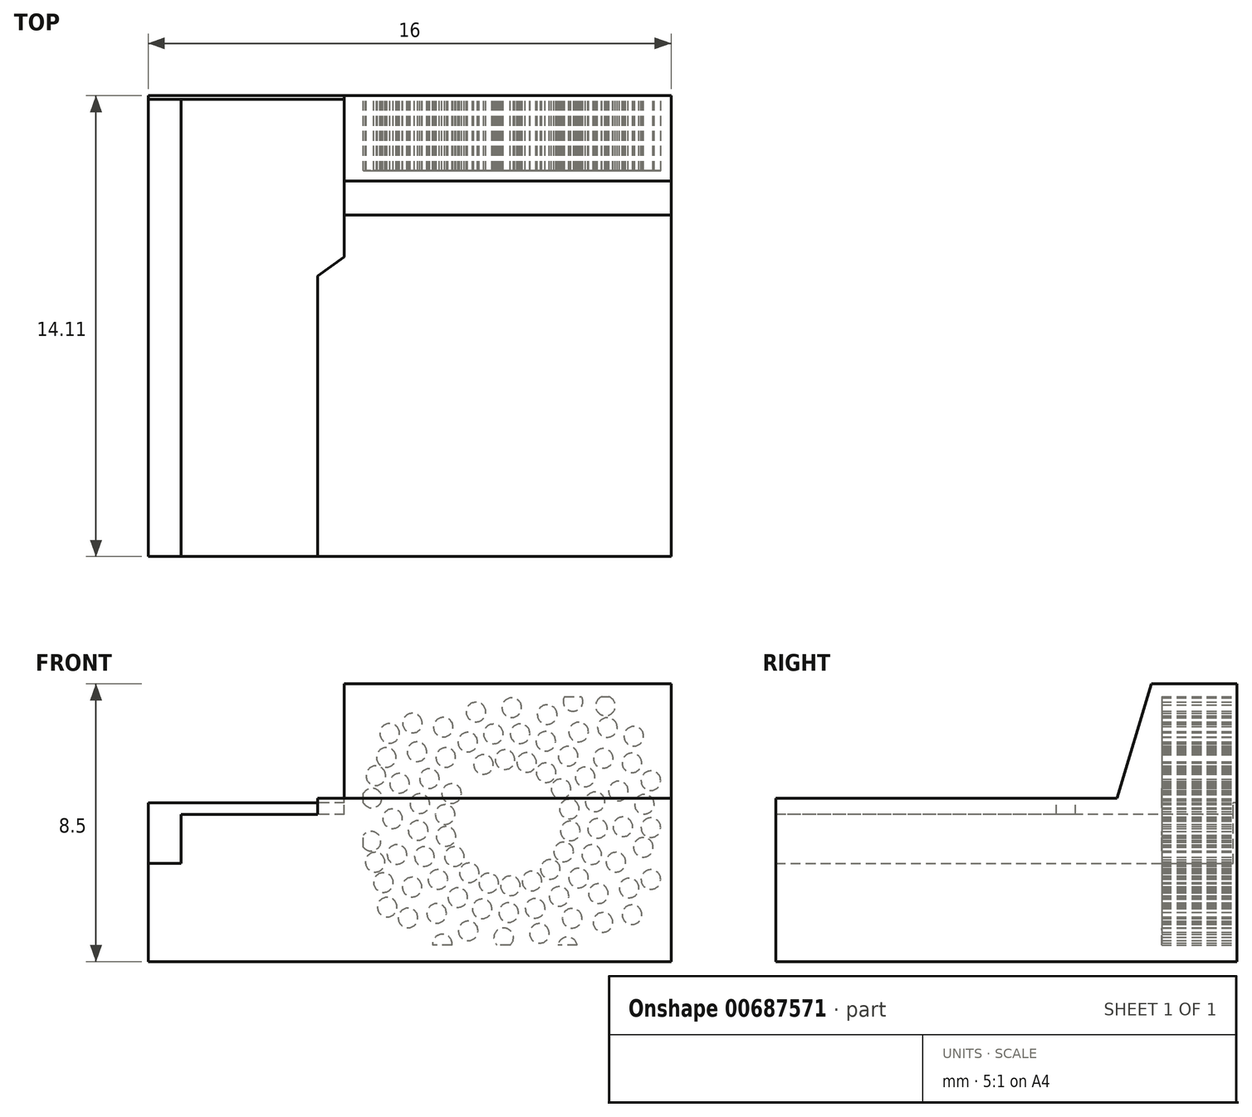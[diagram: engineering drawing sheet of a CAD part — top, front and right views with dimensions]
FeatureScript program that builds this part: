
annotation { "Feature Type Name" : "Feature", "Feature Type Description" : "" }
export const myFeature = defineFeature(function(context is Context, id is Id, definition is map)
    precondition{}
    {
        {
            var Q0;
            Q0=qCreatedBy(makeId("Top.planeOp"),FACE);
            var sketch = newSketch(context, id + "F0", { "sketchPlane" : qUnion([Q0])});
            skLineSegment(sketch, "E0.bottom", {"start": v(0, 0) * mm, "end": v(-16, 0) * mm});
            skLineSegment(sketch, "E0.top", {"start": v(0, 14) * mm, "end": v(-16, 14) * mm});
            skLineSegment(sketch, "E0.left", {"start": v(0, 0) * mm, "end": v(0, 14) * mm});
            skLineSegment(sketch, "E0.right", {"start": v(-16, 0) * mm, "end": v(-16, 14) * mm});
            skSolve(sketch);
        }
        {
            var Q0;
            Q0 = qSketchRegion(id + "F0", true);
            extrude(context, id + "F1", {"entities" : qUnion([Q0]), "depth" : 5 * mm, "offsetDistance" : 25 * mm});
        }
        {
            var Q0;
            Q0=makeQuery(id+"F1.opExtrude","CAP_FACE",FACE,{"disambiguationData":[OSD([sQuery(id+"F0.wireOp",EDGE,"E0.bottom"),sQuery(id+"F0.wireOp",EDGE,"E0.top"),sQuery(id+"F0.wireOp",EDGE,"E0.left"),sQuery(id+"F0.wireOp",EDGE,"E0.right")])],"isStart":false});
            var sketch = newSketch(context, id + "F2", { "sketchPlane" : qUnion([Q0])});
            skLineSegment(sketch, "E1.bottom", {"start": v(-16, 14) * mm, "end": v(-15, 14) * mm});
            skLineSegment(sketch, "E1.top", {"start": v(-16, 0) * mm, "end": v(-15, 0) * mm});
            skLineSegment(sketch, "E1.left", {"start": v(-16, 14) * mm, "end": v(-16, 0) * mm});
            skLineSegment(sketch, "E1.right", {"start": v(-15, 14) * mm, "end": v(-15, 0) * mm});
            skSolve(sketch);
        }
        {
            var Q0;
            Q0=makeQuery(id+"F2.imprint","IMPRINT",FACE,{"disambiguationData":[TD([[makeQuery(id+"F2.imprint","IMPRINT",EDGE,{"derivedFrom":sQuery(id+"F2.wireOp",EDGE,"E1.bottom")}),1.0]])]});
            extrude(context, id + "F3", {"entities" : qUnion([Q0]), "operationType" : NewBodyOperationType.REMOVE, "oppositeDirection" : true, "depth" : 2 * mm, "offsetDistance" : 25 * mm});
        }
        {
            var Q0;
            Q0=makeQuery(id+"F1.opExtrude","CAP_FACE",FACE,{"disambiguationData":[OSD([sQuery(id+"F0.wireOp",EDGE,"E0.bottom"),sQuery(id+"F0.wireOp",EDGE,"E0.top"),sQuery(id+"F0.wireOp",EDGE,"E0.left"),sQuery(id+"F0.wireOp",EDGE,"E0.right")])],"isStart":false});
            var sketch = newSketch(context, id + "F4", { "sketchPlane" : qUnion([Q0])});
            skLineSegment(sketch, "E2", {"start": v(-15, 14) * mm, "end": v(-10, 14) * mm});
            skLineSegment(sketch, "E3", {"start": v(-10, 14) * mm, "end": v(-10, 9.18) * mm});
            skLineSegment(sketch, "E4", {"start": v(-10, 9.18) * mm, "end": v(-10.81, 8.6) * mm});
            skLineSegment(sketch, "E5", {"start": v(-10.81, 8.6) * mm, "end": v(-10.81, 0) * mm});
            skLineSegment(sketch, "E6", {"start": v(-15, 14) * mm, "end": v(-15, 0) * mm});
            skLineSegment(sketch, "E7", {"start": v(-15, 0) * mm, "end": v(-10.81, 0) * mm});
            skSolve(sketch);
        }
        {
            var Q0;
            Q0 = qSketchRegion(id + "F4", true);
            extrude(context, id + "F5", {"entities" : qUnion([Q0]), "operationType" : NewBodyOperationType.REMOVE, "endBound" : BoundingType.SYMMETRIC, "oppositeDirection" : true, "depth" : 1 * mm, "offsetDistance" : 25 * mm});
        }
        {
            var Q0;
            Q0=makeQuery(id+"F1.opExtrude","CAP_FACE",FACE,{"disambiguationData":[OSD([sQuery(id+"F0.wireOp",EDGE,"E0.bottom"),sQuery(id+"F0.wireOp",EDGE,"E0.top"),sQuery(id+"F0.wireOp",EDGE,"E0.left"),sQuery(id+"F0.wireOp",EDGE,"E0.right")])],"isStart":false});
            var sketch = newSketch(context, id + "F6", { "sketchPlane" : qUnion([Q0])});
            skLineSegment(sketch, "E8", {"start": v(0, 14) * mm, "end": v(0, 10) * mm});
            skLineSegment(sketch, "E9", {"start": v(0, 10) * mm, "end": v(-10, 10) * mm});
            skLineSegment(sketch, "E10", {"start": v(-10, 10) * mm, "end": v(-10, 14) * mm});
            skLineSegment(sketch, "E11", {"start": v(-10, 14) * mm, "end": v(0, 14) * mm});
            skSolve(sketch);
        }
        {
            var Q0;
            Q0=makeQuery(id+"F6.imprint","IMPRINT",FACE,{"disambiguationData":[TD([[makeQuery(id+"F6.imprint","IMPRINT",EDGE,{"derivedFrom":sQuery(id+"F6.wireOp",EDGE,"E8")}),1.0]])]});
            extrude(context, id + "F7", {"entities" : qUnion([Q0]), "operationType" : NewBodyOperationType.ADD, "depth" : 3.5 * mm, "offsetDistance" : 25 * mm});
        }
        {
            var Q0;
            Q0=makeQuery(id+"F7.opExtrude","CAP_EDGE",EDGE,{"disambiguationData":[OSD([sQuery(id+"F6.wireOp",EDGE,"E9")])],"isStart":false});
            chamfer(context, id + "F8", {"entities" : qUnion([Q0]), "chamferType" : ChamferType.TWO_OFFSETS, "width1" : 5 * mm, "oppositeDirection" : false, "width2" : 1.5 * mm, "tangentPropagation" : true});
        }
        {
            var Q0;
            Q0=makeQuery(id+"F7.boolean.opBoolean","MERGE",FACE,{"derivedFrom":[makeQuery(id+"F1.opExtrude","SWEPT_FACE",FACE,{"disambiguationData":[OSD([sQuery(id+"F0.wireOp",EDGE,"E0.top")])]}),makeQuery(id+"F7.opExtrude","SWEPT_FACE",FACE,{"disambiguationData":[OSD([sQuery(id+"F6.wireOp",EDGE,"E11")])]})]});
            var sketch = newSketch(context, id + "F9", { "sketchPlane" : qUnion([Q0])});
            skLineSegment(sketch, "E12", {"start": v(10, 4.85) * mm, "end": v(15, 4.85) * mm});
            skLineSegment(sketch, "E13", {"start": v(16, 3) * mm, "end": v(16, 4.85) * mm});
            skLineSegment(sketch, "E14", {"start": v(16, 4.85) * mm, "end": v(15, 4.85) * mm});
            skLineSegment(sketch, "E15", {"start": v(10, 4.85) * mm, "end": v(10, 0) * mm});
            skLineSegment(sketch, "E16", {"start": v(10, 0) * mm, "end": v(16, 0) * mm});
            skLineSegment(sketch, "E17", {"start": v(16, 0) * mm, "end": v(16, 3) * mm});
            skSolve(sketch);
        }
        {
            var Q0;
            Q0 = qSketchRegion(id + "F9", true);
            var Q1;
            {var subQ0=sQuery(id+"F6.wireOp",EDGE,"E11");var subQ1=makeQuery(id+"F7.opExtrude","CAP_EDGE",EDGE,{"disambiguationData":[OSD([subQ0])],"isStart":false});Q1=makeQuery(id+"F9.imprint","IMPRINT",FACE,{"disambiguationData":[TD([[makeQuery(id+"F9.imprint","IMPRINT",EDGE,{"derivedFrom":subQ1}),-1.0]])]});}
            extrude(context, id + "F10", {"entities" : qUnion([Q0, Q1]), "operationType" : NewBodyOperationType.ADD, "depth" : 0.1 * mm, "offsetDistance" : 25 * mm});
        }
        {
            var Q0;
            Q0=makeQuery(id+"F10.opExtrude","CAP_FACE",FACE,{"disambiguationData":[OSD([sQuery(id+"F0.wireOp",EDGE,"E0.top"),sQuery(id+"F0.wireOp",EDGE,"E0.left"),sQuery(id+"F4.wireOp",EDGE,"E2"),sQuery(id+"F4.wireOp",EDGE,"E3"),sQuery(id+"F6.wireOp",EDGE,"E8"),sQuery(id+"F6.wireOp",EDGE,"E10"),sQuery(id+"F6.wireOp",EDGE,"E11"),sQuery(id+"F9.wireOp",EDGE,"E12"),sQuery(id+"F9.wireOp",EDGE,"E13"),sQuery(id+"F9.wireOp",EDGE,"E14"),sQuery(id+"F9.wireOp",EDGE,"E16"),sQuery(id+"F9.wireOp",EDGE,"E17")])],"isStart":false});
            var sketch = newSketch(context, id + "F11", { "sketchPlane" : qUnion([Q0])});
            skCircle(sketch, "E18.cCircle", {"center": v(5, 4.25) * mm, "radius": 1.07 * mm, "construction": true});
            skPoint(sketch, "E18.cCircle.centerSnap0", {"position": v(0, 4.25) * mm});
            skPoint(sketch, "E18.cCircle.centerSnap1", {"position": v(5, 8.5) * mm});
            skLineSegment(sketch, "E18.0", {"start": v(6.23, 4.28) * mm, "end": v(5.64, 3.2) * mm});
            skLineSegment(sketch, "E18.1", {"start": v(5.64, 3.2) * mm, "end": v(4.4, 3.17) * mm});
            skLineSegment(sketch, "E18.2", {"start": v(4.4, 3.17) * mm, "end": v(3.77, 4.22) * mm});
            skLineSegment(sketch, "E18.3", {"start": v(3.77, 4.22) * mm, "end": v(4.36, 5.3) * mm});
            skLineSegment(sketch, "E18.4", {"start": v(4.36, 5.3) * mm, "end": v(5.6, 5.33) * mm});
            skLineSegment(sketch, "E18.5", {"start": v(5.6, 5.33) * mm, "end": v(6.23, 4.28) * mm});
            skPoint(sketch, "E18.0.midPoint", {"position": v(5.94, 3.74) * mm});
            skLineSegment(sketch, "E19", {"start": v(4.98, 8.1) * mm, "end": v(1.66, 8.1) * mm});
            skPoint(sketch, "E19.startSnap0", {"position": v(4.98, 5.32) * mm});
            skLineSegment(sketch, "E20", {"start": v(1.66, 8.1) * mm, "end": v(0.32, 6.97) * mm});
            skLineSegment(sketch, "E21", {"start": v(0.32, 6.97) * mm, "end": v(0.32, 1.53) * mm});
            skLineSegment(sketch, "E22", {"start": v(0.32, 1.53) * mm, "end": v(1.39, 0.5) * mm});
            skLineSegment(sketch, "E23", {"start": v(1.39, 0.5) * mm, "end": v(8.08, 0.5) * mm});
            skLineSegment(sketch, "E24", {"start": v(8.08, 0.5) * mm, "end": v(9.41, 1.53) * mm});
            skLineSegment(sketch, "E25", {"start": v(9.41, 1.53) * mm, "end": v(9.41, 6.97) * mm});
            skLineSegment(sketch, "E26", {"start": v(9.41, 6.97) * mm, "end": v(7.8, 8.1) * mm});
            skLineSegment(sketch, "E27", {"start": v(7.8, 8.1) * mm, "end": v(4.98, 8.1) * mm});
            skCircle(sketch, "E28", {"center": v(2.63, 5.65) * mm, "radius": 0.3 * mm});
            skCircle(sketch, "E29.1.0", {"center": v(2.32, 4.9) * mm, "radius": 0.3 * mm});
            skCircle(sketch, "E29.2.0", {"center": v(2.25, 4.07) * mm, "radius": 0.3 * mm});
            skCircle(sketch, "E30", {"center": v(3.29, 3.36) * mm, "radius": 0.3 * mm});
            skCircle(sketch, "E31.1.0", {"center": v(3.7, 2.82) * mm, "radius": 0.3 * mm});
            skCircle(sketch, "E31.2.0", {"center": v(4.26, 2.46) * mm, "radius": 0.3 * mm});
            skCircle(sketch, "E32.1.3.0", {"center": v(2.43, 3.27) * mm, "radius": 0.3 * mm});
            skCircle(sketch, "E32.1.4.0", {"center": v(2.83, 2.56) * mm, "radius": 0.3 * mm});
            skCircle(sketch, "E32.1.5.0", {"center": v(3.43, 2) * mm, "radius": 0.3 * mm});
            skCircle(sketch, "E33.1.6.0", {"center": v(4.16, 1.63) * mm, "radius": 0.3 * mm});
            skCircle(sketch, "E33.1.7.0", {"center": v(4.97, 1.5) * mm, "radius": 0.3 * mm});
            skCircle(sketch, "E34.1.3.0", {"center": v(4.92, 2.32) * mm, "radius": 0.3 * mm});
            skCircle(sketch, "E34.1.4.0", {"center": v(5.58, 2.4) * mm, "radius": 0.3 * mm});
            skCircle(sketch, "E34.1.5.0", {"center": v(6.18, 2.72) * mm, "radius": 0.3 * mm});
            skCircle(sketch, "E34.1.6.0", {"center": v(6.63, 3.21) * mm, "radius": 0.3 * mm});
            skCircle(sketch, "E34.1.7.0", {"center": v(6.89, 3.83) * mm, "radius": 0.3 * mm});
            skCircle(sketch, "E35.1.8.0", {"center": v(5.78, 1.61) * mm, "radius": 0.3 * mm});
            skCircle(sketch, "E35.1.9.0", {"center": v(6.53, 1.96) * mm, "radius": 0.3 * mm});
            skCircle(sketch, "E35.1.10.0", {"center": v(7.13, 2.51) * mm, "radius": 0.3 * mm});
            skCircle(sketch, "E35.1.11.0", {"center": v(7.55, 3.22) * mm, "radius": 0.3 * mm});
            skCircle(sketch, "E36.1.12.0", {"center": v(7.74, 4.01) * mm, "radius": 0.3 * mm});
            skCircle(sketch, "E36.1.13.0", {"center": v(7.69, 4.83) * mm, "radius": 0.3 * mm});
            skCircle(sketch, "E36.1.14.0", {"center": v(7.4, 5.6) * mm, "radius": 0.3 * mm});
            skCircle(sketch, "E36.1.15.0", {"center": v(6.9, 6.25) * mm, "radius": 0.3 * mm});
            skCircle(sketch, "E36.1.16.0", {"center": v(6.22, 6.72) * mm, "radius": 0.3 * mm});
            skCircle(sketch, "E36.1.17.0", {"center": v(5.44, 6.97) * mm, "radius": 0.3 * mm});
            skCircle(sketch, "E36.1.18.0", {"center": v(4.62, 6.98) * mm, "radius": 0.3 * mm});
            skCircle(sketch, "E36.1.19.0", {"center": v(3.83, 6.74) * mm, "radius": 0.3 * mm});
            skCircle(sketch, "E37.1.8.0", {"center": v(6.92, 4.5) * mm, "radius": 0.3 * mm});
            skCircle(sketch, "E37.1.9.0", {"center": v(6.71, 5.14) * mm, "radius": 0.3 * mm});
            skCircle(sketch, "E37.1.10.0", {"center": v(6.3, 5.68) * mm, "radius": 0.3 * mm});
            skCircle(sketch, "E37.1.11.0", {"center": v(5.74, 6.04) * mm, "radius": 0.3 * mm});
            skCircle(sketch, "E37.1.12.0", {"center": v(5.08, 6.18) * mm, "radius": 0.3 * mm});
            skCircle(sketch, "E37.1.13.0", {"center": v(4.42, 6.1) * mm, "radius": 0.3 * mm});
            skCircle(sketch, "E37.1.14.0", {"center": v(3.82, 5.78) * mm, "radius": 0.3 * mm});
            skCircle(sketch, "E37.1.15.0", {"center": v(3.37, 5.29) * mm, "radius": 0.3 * mm});
            skCircle(sketch, "E37.1.16.0", {"center": v(3.11, 4.67) * mm, "radius": 0.3 * mm});
            skCircle(sketch, "E37.1.17.0", {"center": v(3.08, 4) * mm, "radius": 0.3 * mm});
            skCircle(sketch, "E38.1.20.0", {"center": v(3.15, 6.29) * mm, "radius": 0.3 * mm});
            skCircle(sketch, "E39", {"center": v(3.8, 7.56) * mm, "radius": 0.3 * mm});
            skCircle(sketch, "E40.1.0", {"center": v(2.83, 7.03) * mm, "radius": 0.3 * mm});
            skCircle(sketch, "E40.2.0", {"center": v(2.08, 6.22) * mm, "radius": 0.3 * mm});
            skCircle(sketch, "E41.1.3.0", {"center": v(1.61, 5.22) * mm, "radius": 0.3 * mm});
            skCircle(sketch, "E41.1.4.0", {"center": v(1.48, 4.13) * mm, "radius": 0.3 * mm});
            skCircle(sketch, "E41.1.5.0", {"center": v(1.69, 3.04) * mm, "radius": 0.3 * mm});
            skCircle(sketch, "E41.1.6.0", {"center": v(2.22, 2.08) * mm, "radius": 0.3 * mm});
            skCircle(sketch, "E41.1.7.0", {"center": v(3.03, 1.33) * mm, "radius": 0.3 * mm});
            skCircle(sketch, "E42.1.8.0", {"center": v(4.03, 0.86) * mm, "radius": 0.3 * mm});
            skArc(sketch, "E42.1.9.0", {"start": v(5.33, 0.5) * mm, "mid": v(5.12, 1.03) * mm, "end": v(4.92, 0.5) * mm});
            skCircle(sketch, "E42.1.10.0", {"center": v(6.2, 0.94) * mm, "radius": 0.3 * mm});
            skCircle(sketch, "E42.1.11.0", {"center": v(7.17, 1.47) * mm, "radius": 0.3 * mm});
            skCircle(sketch, "E42.1.12.0", {"center": v(7.92, 2.28) * mm, "radius": 0.3 * mm});
            skCircle(sketch, "E42.1.13.0", {"center": v(8.39, 3.28) * mm, "radius": 0.3 * mm});
            skCircle(sketch, "E42.1.14.0", {"center": v(8.52, 4.37) * mm, "radius": 0.3 * mm});
            skCircle(sketch, "E42.1.15.0", {"center": v(8.31, 5.46) * mm, "radius": 0.3 * mm});
            skCircle(sketch, "E42.1.16.0", {"center": v(7.78, 6.42) * mm, "radius": 0.3 * mm});
            skCircle(sketch, "E42.1.17.0", {"center": v(6.97, 7.17) * mm, "radius": 0.3 * mm});
            skCircle(sketch, "E42.1.18.0", {"center": v(5.97, 7.64) * mm, "radius": 0.3 * mm});
            skCircle(sketch, "E42.1.19.0", {"center": v(4.88, 7.77) * mm, "radius": 0.3 * mm});
            skArc(sketch, "E43", {"start": v(2.74, 8.1) * mm, "mid": v(3, 7.67) * mm, "end": v(3.27, 8.1) * mm});
            skCircle(sketch, "E44.1.0", {"center": v(1.95, 7.17) * mm, "radius": 0.3 * mm});
            skCircle(sketch, "E44.2.0", {"center": v(1.2, 6.08) * mm, "radius": 0.3 * mm});
            skCircle(sketch, "E45.1.3.0", {"center": v(0.82, 4.82) * mm, "radius": 0.3 * mm});
            skCircle(sketch, "E45.1.4.0", {"center": v(0.85, 3.5) * mm, "radius": 0.3 * mm});
            skCircle(sketch, "E45.1.5.0", {"center": v(1.28, 2.25) * mm, "radius": 0.3 * mm});
            skCircle(sketch, "E45.1.6.0", {"center": v(2.08, 1.2) * mm, "radius": 0.3 * mm});
            skArc(sketch, "E45.1.7.0", {"start": v(3.46, 0.5) * mm, "mid": v(3.17, 0.75) * mm, "end": v(2.87, 0.5) * mm});
            skArc(sketch, "E45.1.10.0", {"start": v(7.3, 0.5) * mm, "mid": v(7, 0.83) * mm, "end": v(6.7, 0.5) * mm});
            skCircle(sketch, "E45.1.11.0", {"center": v(8.05, 1.33) * mm, "radius": 0.3 * mm});
            skCircle(sketch, "E45.1.12.0", {"center": v(8.8, 2.42) * mm, "radius": 0.3 * mm});
            skArc(sketch, "E45.1.13.0", {"start": v(9.41, 3.87) * mm, "mid": v(8.88, 3.68) * mm, "end": v(9.41, 3.5) * mm});
            skArc(sketch, "E45.1.14.0", {"start": v(9.41, 5.15) * mm, "mid": v(8.85, 5) * mm, "end": v(9.41, 4.86) * mm});
            skCircle(sketch, "E45.1.15.0", {"center": v(8.72, 6.25) * mm, "radius": 0.3 * mm});
            skCircle(sketch, "E45.1.16.0", {"center": v(7.92, 7.3) * mm, "radius": 0.3 * mm});
            skArc(sketch, "E45.1.17.0", {"start": v(6.54, 8.1) * mm, "mid": v(6.83, 7.75) * mm, "end": v(7.13, 8.1) * mm});
            skArc(sketch, "E45.1.19.0", {"start": v(4.2, 8.1) * mm, "mid": v(4.25, 8.1) * mm, "end": v(4.3, 8.1) * mm});
            skCircle(sketch, "E46", {"center": v(1.14, 6.9) * mm, "radius": 0.3 * mm});
            skCircle(sketch, "E47", {"center": v(8.61, 6.99) * mm, "radius": 0.3 * mm});
            skCircle(sketch, "E48", {"center": v(8.69, 1.67) * mm, "radius": 0.3 * mm});
            skCircle(sketch, "E49", {"center": v(1.2, 1.43) * mm, "radius": 0.3 * mm});
            skCircle(sketch, "E50", {"center": v(2, 7.83) * mm, "radius": 0.3 * mm});
            skCircle(sketch, "E51", {"center": v(0.62, 5.54) * mm, "radius": 0.3 * mm});
            skCircle(sketch, "E52", {"center": v(9.04, 5.7) * mm, "radius": 0.3 * mm});
            skCircle(sketch, "E53", {"center": v(0.62, 2.51) * mm, "radius": 0.3 * mm});
            skCircle(sketch, "E54", {"center": v(0.62, 4.1) * mm, "radius": 0.3 * mm});
            skCircle(sketch, "E55", {"center": v(9.05, 3.04) * mm, "radius": 0.3 * mm});
            skSolve(sketch);
        }
        {
            var Q0;
            Q0=makeQuery(id+"F11.imprint","IMPRINT",FACE,{"disambiguationData":[TD([[makeQuery(id+"F11.imprint","IMPRINT",EDGE,{"derivedFrom":sQuery(id+"F11.wireOp",EDGE,"E44.1.0")}),1.0]])]});
            var Q1;
            Q1=makeQuery(id+"F11.imprint","IMPRINT",FACE,{"disambiguationData":[TD([[makeQuery(id+"F11.imprint","IMPRINT",EDGE,{"derivedFrom":sQuery(id+"F11.wireOp",EDGE,"E40.1.0")}),1.0]])]});
            var Q2;
            Q2=makeQuery(id+"F11.imprint","IMPRINT",FACE,{"disambiguationData":[TD([[makeQuery(id+"F11.imprint","IMPRINT",EDGE,{"derivedFrom":sQuery(id+"F11.wireOp",EDGE,"E42.1.19.0")}),1.0]])]});
            var Q3;
            Q3=makeQuery(id+"F11.imprint","IMPRINT",FACE,{"disambiguationData":[TD([[makeQuery(id+"F11.imprint","IMPRINT",EDGE,{"derivedFrom":sQuery(id+"F11.wireOp",EDGE,"E38.1.20.0")}),1.0]])]});
            var Q4;
            Q4=makeQuery(id+"F11.imprint","IMPRINT",FACE,{"disambiguationData":[TD([[makeQuery(id+"F11.imprint","IMPRINT",EDGE,{"derivedFrom":sQuery(id+"F11.wireOp",EDGE,"E40.2.0")}),1.0]])]});
            var Q5;
            Q5=makeQuery(id+"F11.imprint","IMPRINT",FACE,{"disambiguationData":[TD([[makeQuery(id+"F11.imprint","IMPRINT",EDGE,{"derivedFrom":sQuery(id+"F11.wireOp",EDGE,"E53")}),1.0]])]});
            var Q6;
            Q6=makeQuery(id+"F11.imprint","IMPRINT",FACE,{"disambiguationData":[TD([[makeQuery(id+"F11.imprint","IMPRINT",EDGE,{"derivedFrom":sQuery(id+"F11.wireOp",EDGE,"E45.1.5.0")}),1.0]])]});
            var Q7;
            Q7=makeQuery(id+"F11.imprint","IMPRINT",FACE,{"disambiguationData":[TD([[makeQuery(id+"F11.imprint","IMPRINT",EDGE,{"derivedFrom":sQuery(id+"F11.wireOp",EDGE,"E41.1.6.0")}),1.0]])]});
            var Q8;
            Q8=makeQuery(id+"F11.imprint","IMPRINT",FACE,{"disambiguationData":[TD([[makeQuery(id+"F11.imprint","IMPRINT",EDGE,{"derivedFrom":sQuery(id+"F11.wireOp",EDGE,"E41.1.5.0")}),1.0]])]});
            var Q9;
            Q9=makeQuery(id+"F11.imprint","IMPRINT",FACE,{"disambiguationData":[TD([[makeQuery(id+"F11.imprint","IMPRINT",EDGE,{"derivedFrom":sQuery(id+"F11.wireOp",EDGE,"E29.2.0")}),1.0]])]});
            var Q10;
            Q10=makeQuery(id+"F11.imprint","IMPRINT",FACE,{"disambiguationData":[TD([[makeQuery(id+"F11.imprint","IMPRINT",EDGE,{"derivedFrom":sQuery(id+"F11.wireOp",EDGE,"E29.1.0")}),1.0]])]});
            var Q11;
            Q11=makeQuery(id+"F11.imprint","IMPRINT",FACE,{"disambiguationData":[TD([[makeQuery(id+"F11.imprint","IMPRINT",EDGE,{"derivedFrom":sQuery(id+"F11.wireOp",EDGE,"E28")}),1.0]])]});
            var Q12;
            Q12=makeQuery(id+"F11.imprint","IMPRINT",FACE,{"disambiguationData":[TD([[makeQuery(id+"F11.imprint","IMPRINT",EDGE,{"derivedFrom":sQuery(id+"F11.wireOp",EDGE,"E41.1.4.0")}),1.0]])]});
            var Q13;
            Q13=makeQuery(id+"F11.imprint","IMPRINT",FACE,{"disambiguationData":[TD([[makeQuery(id+"F11.imprint","IMPRINT",EDGE,{"derivedFrom":sQuery(id+"F11.wireOp",EDGE,"E54")}),1.0]])]});
            var Q14;
            Q14=makeQuery(id+"F11.imprint","IMPRINT",FACE,{"disambiguationData":[TD([[makeQuery(id+"F11.imprint","IMPRINT",EDGE,{"derivedFrom":sQuery(id+"F11.wireOp",EDGE,"E45.1.4.0")}),1.0]])]});
            var Q15;
            Q15=makeQuery(id+"F11.imprint","IMPRINT",FACE,{"disambiguationData":[TD([[makeQuery(id+"F11.imprint","IMPRINT",EDGE,{"derivedFrom":sQuery(id+"F11.wireOp",EDGE,"E45.1.3.0")}),1.0]])]});
            var Q16;
            Q16=makeQuery(id+"F11.imprint","IMPRINT",FACE,{"disambiguationData":[TD([[makeQuery(id+"F11.imprint","IMPRINT",EDGE,{"derivedFrom":sQuery(id+"F11.wireOp",EDGE,"E51")}),1.0]])]});
            var Q17;
            Q17=makeQuery(id+"F11.imprint","IMPRINT",FACE,{"disambiguationData":[TD([[makeQuery(id+"F11.imprint","IMPRINT",EDGE,{"derivedFrom":sQuery(id+"F11.wireOp",EDGE,"E44.2.0")}),1.0]])]});
            var Q18;
            {var subQ0=sQuery(id+"F11.wireOp",EDGE,"E43");Q18=makeQuery(id+"F11.imprint","IMPRINT",FACE,{"disambiguationData":[TD([[makeQuery(id+"F11.imprint","IMPRINT",EDGE,{"derivedFrom":subQ0}),1.0]])]});}
            var Q19;
            {var subQ0=sQuery(id+"F11.wireOp",EDGE,"E50");var subQ1=sQuery(id+"F11.wireOp",EDGE,"E19");var subQ2=makeQuery(id+"F11.imprint","INTERSECT",VERTEX,{"disambiguationData":[OD(0.0)],"derivedFrom":[subQ1,subQ0]});Q19=makeQuery(id+"F11.imprint","IMPRINT",FACE,{"disambiguationData":[TD([[makeQuery(id+"F11.imprint","IMPRINT",EDGE,{"disambiguationData":[TD([[subQ2,-1.0]])],"derivedFrom":subQ1}),1.0]])]});}
            var Q20;
            Q20=makeQuery(id+"F11.imprint","IMPRINT",FACE,{"disambiguationData":[TD([[makeQuery(id+"F11.imprint","IMPRINT",EDGE,{"derivedFrom":sQuery(id+"F11.wireOp",EDGE,"E39")}),1.0]])]});
            var Q21;
            Q21=makeQuery(id+"F11.imprint","IMPRINT",FACE,{"disambiguationData":[TD([[makeQuery(id+"F11.imprint","IMPRINT",EDGE,{"derivedFrom":sQuery(id+"F11.wireOp",EDGE,"E36.1.18.0")}),1.0]])]});
            var Q22;
            Q22=makeQuery(id+"F11.imprint","IMPRINT",FACE,{"disambiguationData":[TD([[makeQuery(id+"F11.imprint","IMPRINT",EDGE,{"derivedFrom":sQuery(id+"F11.wireOp",EDGE,"E37.1.15.0")}),1.0]])]});
            var Q23;
            Q23=makeQuery(id+"F11.imprint","IMPRINT",FACE,{"disambiguationData":[TD([[makeQuery(id+"F11.imprint","IMPRINT",EDGE,{"derivedFrom":sQuery(id+"F11.wireOp",EDGE,"E37.1.16.0")}),1.0]])]});
            var Q24;
            Q24=makeQuery(id+"F11.imprint","IMPRINT",FACE,{"disambiguationData":[TD([[makeQuery(id+"F11.imprint","IMPRINT",EDGE,{"derivedFrom":sQuery(id+"F11.wireOp",EDGE,"E37.1.14.0")}),1.0]])]});
            var Q25;
            Q25=makeQuery(id+"F11.imprint","IMPRINT",FACE,{"disambiguationData":[TD([[makeQuery(id+"F11.imprint","IMPRINT",EDGE,{"derivedFrom":sQuery(id+"F11.wireOp",EDGE,"E37.1.17.0")}),1.0]])]});
            var Q26;
            Q26=makeQuery(id+"F11.imprint","IMPRINT",FACE,{"disambiguationData":[TD([[makeQuery(id+"F11.imprint","IMPRINT",EDGE,{"derivedFrom":sQuery(id+"F11.wireOp",EDGE,"E30")}),1.0]])]});
            var Q27;
            Q27=makeQuery(id+"F11.imprint","IMPRINT",FACE,{"disambiguationData":[TD([[makeQuery(id+"F11.imprint","IMPRINT",EDGE,{"derivedFrom":sQuery(id+"F11.wireOp",EDGE,"E32.1.4.0")}),1.0]])]});
            var Q28;
            Q28=makeQuery(id+"F11.imprint","IMPRINT",FACE,{"disambiguationData":[TD([[makeQuery(id+"F11.imprint","IMPRINT",EDGE,{"derivedFrom":sQuery(id+"F11.wireOp",EDGE,"E32.1.5.0")}),1.0]])]});
            var Q29;
            Q29=makeQuery(id+"F11.imprint","IMPRINT",FACE,{"disambiguationData":[TD([[makeQuery(id+"F11.imprint","IMPRINT",EDGE,{"derivedFrom":sQuery(id+"F11.wireOp",EDGE,"E45.1.6.0")}),1.0]])]});
            var Q30;
            Q30=makeQuery(id+"F11.imprint","IMPRINT",FACE,{"disambiguationData":[TD([[makeQuery(id+"F11.imprint","IMPRINT",EDGE,{"derivedFrom":sQuery(id+"F11.wireOp",EDGE,"E41.1.7.0")}),1.0]])]});
            var Q31;
            {var subQ0=sQuery(id+"F11.wireOp",EDGE,"E45.1.7.0");Q31=makeQuery(id+"F11.imprint","IMPRINT",FACE,{"disambiguationData":[TD([[makeQuery(id+"F11.imprint","IMPRINT",EDGE,{"derivedFrom":subQ0}),1.0]])]});}
            var Q32;
            Q32=makeQuery(id+"F11.imprint","IMPRINT",FACE,{"disambiguationData":[TD([[makeQuery(id+"F11.imprint","IMPRINT",EDGE,{"derivedFrom":sQuery(id+"F11.wireOp",EDGE,"E42.1.8.0")}),1.0]])]});
            var Q33;
            Q33=makeQuery(id+"F11.imprint","IMPRINT",FACE,{"disambiguationData":[TD([[makeQuery(id+"F11.imprint","IMPRINT",EDGE,{"derivedFrom":sQuery(id+"F11.wireOp",EDGE,"E31.2.0")}),1.0]])]});
            var Q34;
            Q34=makeQuery(id+"F11.imprint","IMPRINT",FACE,{"disambiguationData":[TD([[makeQuery(id+"F11.imprint","IMPRINT",EDGE,{"derivedFrom":sQuery(id+"F11.wireOp",EDGE,"E34.1.3.0")}),1.0]])]});
            var Q35;
            Q35=makeQuery(id+"F11.imprint","IMPRINT",FACE,{"disambiguationData":[TD([[makeQuery(id+"F11.imprint","IMPRINT",EDGE,{"derivedFrom":sQuery(id+"F11.wireOp",EDGE,"E34.1.5.0")}),1.0]])]});
            var Q36;
            Q36=makeQuery(id+"F11.imprint","IMPRINT",FACE,{"disambiguationData":[TD([[makeQuery(id+"F11.imprint","IMPRINT",EDGE,{"derivedFrom":sQuery(id+"F11.wireOp",EDGE,"E34.1.6.0")}),1.0]])]});
            var Q37;
            Q37=makeQuery(id+"F11.imprint","IMPRINT",FACE,{"disambiguationData":[TD([[makeQuery(id+"F11.imprint","IMPRINT",EDGE,{"derivedFrom":sQuery(id+"F11.wireOp",EDGE,"E34.1.7.0")}),1.0]])]});
            var Q38;
            Q38=makeQuery(id+"F11.imprint","IMPRINT",FACE,{"disambiguationData":[TD([[makeQuery(id+"F11.imprint","IMPRINT",EDGE,{"derivedFrom":sQuery(id+"F11.wireOp",EDGE,"E37.1.8.0")}),1.0]])]});
            var Q39;
            Q39=makeQuery(id+"F11.imprint","IMPRINT",FACE,{"disambiguationData":[TD([[makeQuery(id+"F11.imprint","IMPRINT",EDGE,{"derivedFrom":sQuery(id+"F11.wireOp",EDGE,"E37.1.9.0")}),1.0]])]});
            var Q40;
            Q40=makeQuery(id+"F11.imprint","IMPRINT",FACE,{"disambiguationData":[TD([[makeQuery(id+"F11.imprint","IMPRINT",EDGE,{"derivedFrom":sQuery(id+"F11.wireOp",EDGE,"E37.1.11.0")}),1.0]])]});
            var Q41;
            Q41=makeQuery(id+"F11.imprint","IMPRINT",FACE,{"disambiguationData":[TD([[makeQuery(id+"F11.imprint","IMPRINT",EDGE,{"derivedFrom":sQuery(id+"F11.wireOp",EDGE,"E37.1.12.0")}),1.0]])]});
            var Q42;
            Q42=makeQuery(id+"F11.imprint","IMPRINT",FACE,{"disambiguationData":[TD([[makeQuery(id+"F11.imprint","IMPRINT",EDGE,{"derivedFrom":sQuery(id+"F11.wireOp",EDGE,"E37.1.13.0")}),1.0]])]});
            var Q43;
            Q43=makeQuery(id+"F11.imprint","IMPRINT",FACE,{"disambiguationData":[TD([[makeQuery(id+"F11.imprint","IMPRINT",EDGE,{"derivedFrom":sQuery(id+"F11.wireOp",EDGE,"E42.1.17.0")}),1.0]])]});
            var Q44;
            Q44=makeQuery(id+"F11.imprint","IMPRINT",FACE,{"disambiguationData":[TD([[makeQuery(id+"F11.imprint","IMPRINT",EDGE,{"derivedFrom":sQuery(id+"F11.wireOp",EDGE,"E36.1.16.0")}),1.0]])]});
            var Q45;
            Q45=makeQuery(id+"F11.imprint","IMPRINT",FACE,{"disambiguationData":[TD([[makeQuery(id+"F11.imprint","IMPRINT",EDGE,{"derivedFrom":sQuery(id+"F11.wireOp",EDGE,"E45.1.16.0")}),1.0]])]});
            var Q46;
            Q46=makeQuery(id+"F11.imprint","IMPRINT",FACE,{"disambiguationData":[TD([[makeQuery(id+"F11.imprint","IMPRINT",EDGE,{"derivedFrom":sQuery(id+"F11.wireOp",EDGE,"E47")}),1.0]])]});
            var Q47;
            Q47=makeQuery(id+"F11.imprint","IMPRINT",FACE,{"disambiguationData":[TD([[makeQuery(id+"F11.imprint","IMPRINT",EDGE,{"derivedFrom":sQuery(id+"F11.wireOp",EDGE,"E42.1.16.0")}),1.0]])]});
            var Q48;
            Q48=makeQuery(id+"F11.imprint","IMPRINT",FACE,{"disambiguationData":[TD([[makeQuery(id+"F11.imprint","IMPRINT",EDGE,{"derivedFrom":sQuery(id+"F11.wireOp",EDGE,"E36.1.15.0")}),1.0]])]});
            var Q49;
            Q49=makeQuery(id+"F11.imprint","IMPRINT",FACE,{"disambiguationData":[TD([[makeQuery(id+"F11.imprint","IMPRINT",EDGE,{"derivedFrom":sQuery(id+"F11.wireOp",EDGE,"E36.1.14.0")}),1.0]])]});
            var Q50;
            Q50=makeQuery(id+"F11.imprint","IMPRINT",FACE,{"disambiguationData":[TD([[makeQuery(id+"F11.imprint","IMPRINT",EDGE,{"derivedFrom":sQuery(id+"F11.wireOp",EDGE,"E45.1.15.0")}),1.0]])]});
            var Q51;
            Q51=makeQuery(id+"F11.imprint","IMPRINT",FACE,{"disambiguationData":[TD([[makeQuery(id+"F11.imprint","IMPRINT",EDGE,{"derivedFrom":sQuery(id+"F11.wireOp",EDGE,"E52")}),1.0]])]});
            var Q52;
            Q52=makeQuery(id+"F11.imprint","IMPRINT",FACE,{"disambiguationData":[TD([[makeQuery(id+"F11.imprint","IMPRINT",EDGE,{"derivedFrom":sQuery(id+"F11.wireOp",EDGE,"E42.1.15.0")}),1.0]])]});
            var Q53;
            Q53=makeQuery(id+"F11.imprint","IMPRINT",FACE,{"disambiguationData":[TD([[makeQuery(id+"F11.imprint","IMPRINT",EDGE,{"derivedFrom":sQuery(id+"F11.wireOp",EDGE,"E36.1.13.0")}),1.0]])]});
            var Q54;
            {var subQ0=sQuery(id+"F11.wireOp",EDGE,"E45.1.14.0");Q54=makeQuery(id+"F11.imprint","IMPRINT",FACE,{"disambiguationData":[TD([[makeQuery(id+"F11.imprint","IMPRINT",EDGE,{"derivedFrom":subQ0}),1.0]])]});}
            var Q55;
            Q55=makeQuery(id+"F11.imprint","IMPRINT",FACE,{"disambiguationData":[TD([[makeQuery(id+"F11.imprint","IMPRINT",EDGE,{"derivedFrom":sQuery(id+"F11.wireOp",EDGE,"E36.1.12.0")}),1.0]])]});
            var Q56;
            Q56=makeQuery(id+"F11.imprint","IMPRINT",FACE,{"disambiguationData":[TD([[makeQuery(id+"F11.imprint","IMPRINT",EDGE,{"derivedFrom":sQuery(id+"F11.wireOp",EDGE,"E35.1.11.0")}),1.0]])]});
            var Q57;
            Q57=makeQuery(id+"F11.imprint","IMPRINT",FACE,{"disambiguationData":[TD([[makeQuery(id+"F11.imprint","IMPRINT",EDGE,{"derivedFrom":sQuery(id+"F11.wireOp",EDGE,"E42.1.12.0")}),1.0]])]});
            var Q58;
            Q58=makeQuery(id+"F11.imprint","IMPRINT",FACE,{"disambiguationData":[TD([[makeQuery(id+"F11.imprint","IMPRINT",EDGE,{"derivedFrom":sQuery(id+"F11.wireOp",EDGE,"E35.1.10.0")}),1.0]])]});
            var Q59;
            Q59=makeQuery(id+"F11.imprint","IMPRINT",FACE,{"disambiguationData":[TD([[makeQuery(id+"F11.imprint","IMPRINT",EDGE,{"derivedFrom":sQuery(id+"F11.wireOp",EDGE,"E45.1.12.0")}),1.0]])]});
            var Q60;
            Q60=makeQuery(id+"F11.imprint","IMPRINT",FACE,{"disambiguationData":[TD([[makeQuery(id+"F11.imprint","IMPRINT",EDGE,{"derivedFrom":sQuery(id+"F11.wireOp",EDGE,"E48")}),1.0]])]});
            var Q61;
            Q61=makeQuery(id+"F11.imprint","IMPRINT",FACE,{"disambiguationData":[TD([[makeQuery(id+"F11.imprint","IMPRINT",EDGE,{"derivedFrom":sQuery(id+"F11.wireOp",EDGE,"E45.1.11.0")}),1.0]])]});
            var Q62;
            Q62=makeQuery(id+"F11.imprint","IMPRINT",FACE,{"disambiguationData":[TD([[makeQuery(id+"F11.imprint","IMPRINT",EDGE,{"derivedFrom":sQuery(id+"F11.wireOp",EDGE,"E42.1.11.0")}),1.0]])]});
            var Q63;
            Q63=makeQuery(id+"F11.imprint","IMPRINT",FACE,{"disambiguationData":[TD([[makeQuery(id+"F11.imprint","IMPRINT",EDGE,{"derivedFrom":sQuery(id+"F11.wireOp",EDGE,"E35.1.8.0")}),1.0]])]});
            var Q64;
            Q64=makeQuery(id+"F11.imprint","IMPRINT",FACE,{"disambiguationData":[TD([[makeQuery(id+"F11.imprint","IMPRINT",EDGE,{"derivedFrom":sQuery(id+"F11.wireOp",EDGE,"E33.1.7.0")}),1.0]])]});
            var Q65;
            {var subQ0=sQuery(id+"F11.wireOp",EDGE,"E42.1.9.0");Q65=makeQuery(id+"F11.imprint","IMPRINT",FACE,{"disambiguationData":[TD([[makeQuery(id+"F11.imprint","IMPRINT",EDGE,{"derivedFrom":subQ0}),1.0]])]});}
            var Q66;
            {var subQ0=sQuery(id+"F11.wireOp",EDGE,"E45.1.10.0");Q66=makeQuery(id+"F11.imprint","IMPRINT",FACE,{"disambiguationData":[TD([[makeQuery(id+"F11.imprint","IMPRINT",EDGE,{"derivedFrom":subQ0}),1.0]])]});}
            var Q67;
            Q67=makeQuery(id+"F11.imprint","IMPRINT",FACE,{"disambiguationData":[TD([[makeQuery(id+"F11.imprint","IMPRINT",EDGE,{"derivedFrom":sQuery(id+"F11.wireOp",EDGE,"E42.1.10.0")}),1.0]])]});
            var Q68;
            Q68=makeQuery(id+"F11.imprint","IMPRINT",FACE,{"disambiguationData":[TD([[makeQuery(id+"F11.imprint","IMPRINT",EDGE,{"derivedFrom":sQuery(id+"F11.wireOp",EDGE,"E35.1.9.0")}),1.0]])]});
            var Q69;
            Q69=makeQuery(id+"F11.imprint","IMPRINT",FACE,{"disambiguationData":[TD([[makeQuery(id+"F11.imprint","IMPRINT",EDGE,{"derivedFrom":sQuery(id+"F11.wireOp",EDGE,"E34.1.4.0")}),1.0]])]});
            var Q70;
            Q70=makeQuery(id+"F11.imprint","IMPRINT",FACE,{"disambiguationData":[TD([[makeQuery(id+"F11.imprint","IMPRINT",EDGE,{"derivedFrom":sQuery(id+"F11.wireOp",EDGE,"E33.1.6.0")}),1.0]])]});
            var Q71;
            Q71=makeQuery(id+"F11.imprint","IMPRINT",FACE,{"disambiguationData":[TD([[makeQuery(id+"F11.imprint","IMPRINT",EDGE,{"derivedFrom":sQuery(id+"F11.wireOp",EDGE,"E55")}),1.0]])]});
            var Q72;
            Q72=makeQuery(id+"F11.imprint","IMPRINT",FACE,{"disambiguationData":[TD([[makeQuery(id+"F11.imprint","IMPRINT",EDGE,{"derivedFrom":sQuery(id+"F11.wireOp",EDGE,"E42.1.13.0")}),1.0]])]});
            var Q73;
            {var subQ0=sQuery(id+"F11.wireOp",EDGE,"E45.1.13.0");Q73=makeQuery(id+"F11.imprint","IMPRINT",FACE,{"disambiguationData":[TD([[makeQuery(id+"F11.imprint","IMPRINT",EDGE,{"derivedFrom":subQ0}),1.0]])]});}
            var Q74;
            Q74=makeQuery(id+"F11.imprint","IMPRINT",FACE,{"disambiguationData":[TD([[makeQuery(id+"F11.imprint","IMPRINT",EDGE,{"derivedFrom":sQuery(id+"F11.wireOp",EDGE,"E42.1.14.0")}),1.0]])]});
            var Q75;
            Q75=makeQuery(id+"F11.imprint","IMPRINT",FACE,{"disambiguationData":[TD([[makeQuery(id+"F11.imprint","IMPRINT",EDGE,{"derivedFrom":sQuery(id+"F11.wireOp",EDGE,"E31.1.0")}),1.0]])]});
            var Q76;
            Q76=makeQuery(id+"F11.imprint","IMPRINT",FACE,{"disambiguationData":[TD([[makeQuery(id+"F11.imprint","IMPRINT",EDGE,{"derivedFrom":sQuery(id+"F11.wireOp",EDGE,"E49")}),1.0]])]});
            var Q77;
            Q77=makeQuery(id+"F11.imprint","IMPRINT",FACE,{"disambiguationData":[TD([[makeQuery(id+"F11.imprint","IMPRINT",EDGE,{"derivedFrom":sQuery(id+"F11.wireOp",EDGE,"E32.1.3.0")}),1.0]])]});
            var Q78;
            Q78=makeQuery(id+"F11.imprint","IMPRINT",FACE,{"disambiguationData":[TD([[makeQuery(id+"F11.imprint","IMPRINT",EDGE,{"derivedFrom":sQuery(id+"F11.wireOp",EDGE,"E41.1.3.0")}),1.0]])]});
            var Q79;
            Q79=makeQuery(id+"F11.imprint","IMPRINT",FACE,{"disambiguationData":[TD([[makeQuery(id+"F11.imprint","IMPRINT",EDGE,{"derivedFrom":sQuery(id+"F11.wireOp",EDGE,"E46")}),1.0]])]});
            var Q80;
            Q80=makeQuery(id+"F11.imprint","IMPRINT",FACE,{"disambiguationData":[TD([[makeQuery(id+"F11.imprint","IMPRINT",EDGE,{"derivedFrom":sQuery(id+"F11.wireOp",EDGE,"E36.1.19.0")}),1.0]])]});
            var Q81;
            Q81=makeQuery(id+"F11.imprint","IMPRINT",FACE,{"disambiguationData":[TD([[makeQuery(id+"F11.imprint","IMPRINT",EDGE,{"derivedFrom":sQuery(id+"F11.wireOp",EDGE,"E36.1.17.0")}),1.0]])]});
            var Q82;
            Q82=makeQuery(id+"F11.imprint","IMPRINT",FACE,{"disambiguationData":[TD([[makeQuery(id+"F11.imprint","IMPRINT",EDGE,{"derivedFrom":sQuery(id+"F11.wireOp",EDGE,"E42.1.18.0")}),1.0]])]});
            extrude(context, id + "F12", {"entities" : qUnion([Q0, Q1, Q2, Q3, Q4, Q5, Q6, Q7, Q8, Q9, Q10, Q11, Q12, Q13, Q14, Q15, Q16, Q17, Q18, Q19, Q20, Q21, Q22, Q23, Q24, Q25, Q26, Q27, Q28, Q29, Q30, Q31, Q32, Q33, Q34, Q35, Q36, Q37, Q38, Q39, Q40, Q41, Q42, Q43, Q44, Q45, Q46, Q47, Q48, Q49, Q50, Q51, Q52, Q53, Q54, Q55, Q56, Q57, Q58, Q59, Q60, Q61, Q62, Q63, Q64, Q65, Q66, Q67, Q68, Q69, Q70, Q71, Q72, Q73, Q74, Q75, Q76, Q77, Q78, Q79, Q80, Q81, Q82]), "operationType" : NewBodyOperationType.REMOVE, "oppositeDirection" : true, "depth" : 2.3 * mm, "offsetDistance" : 25 * mm});
        }
    });
